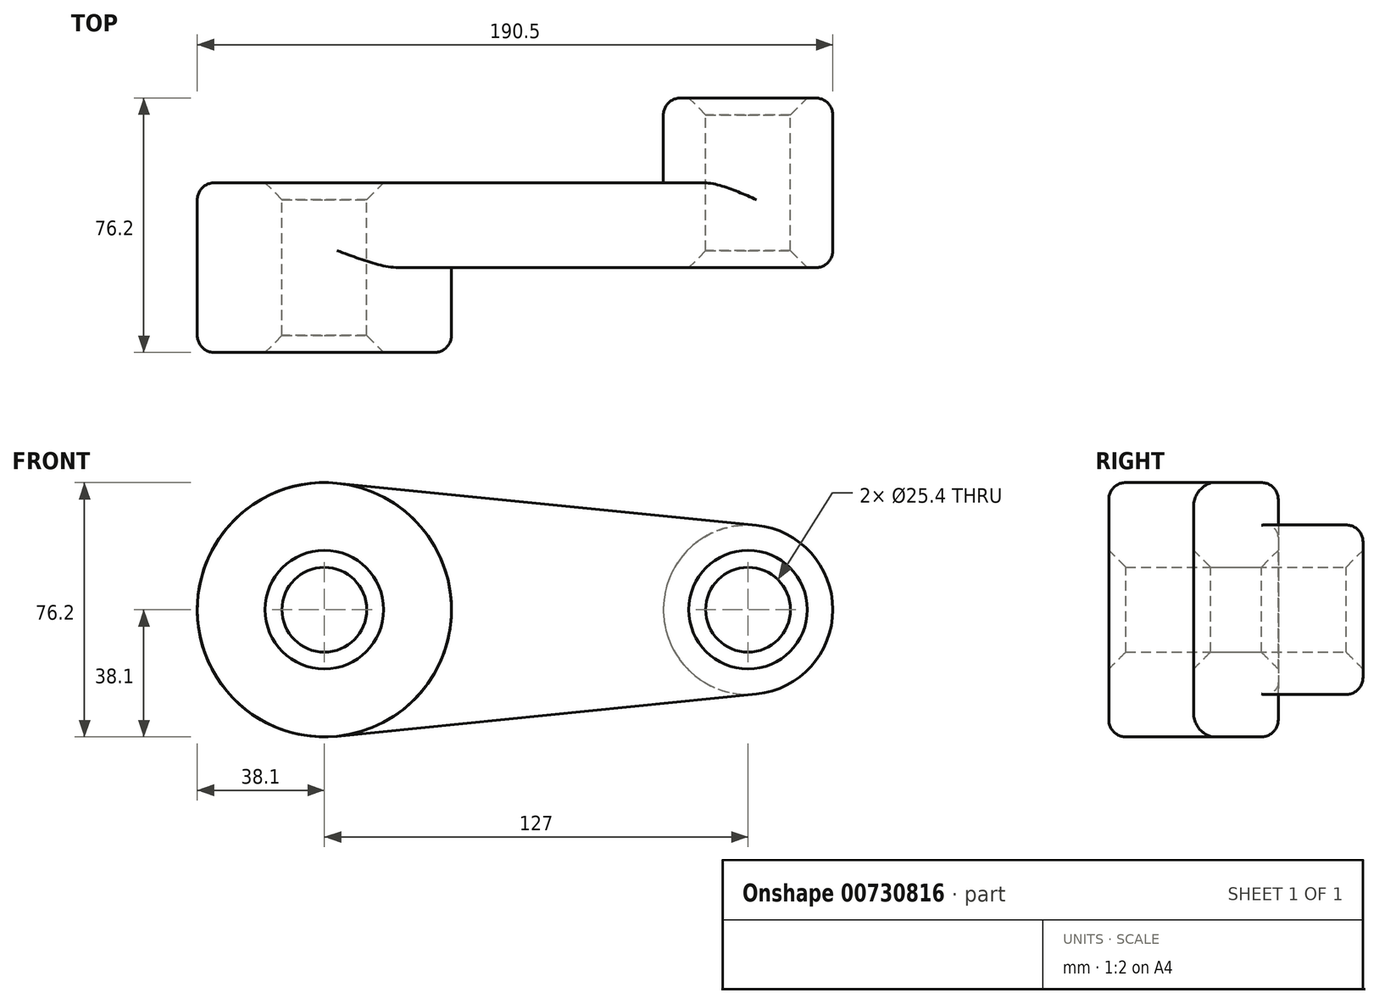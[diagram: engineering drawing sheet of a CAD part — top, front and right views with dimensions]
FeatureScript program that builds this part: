
annotation { "Feature Type Name" : "Feature", "Feature Type Description" : "" }
export const myFeature = defineFeature(function(context is Context, id is Id, definition is map)
    precondition{}
    {
        {
            var Q0;
            Q0=qCreatedBy(makeId("Front.planeOp"),FACE);
            var sketch = newSketch(context, id + "F0", { "sketchPlane" : qUnion([Q0])});
            skCircle(sketch, "E0", {"center": v(0, 0) * mm, "radius": 38.1 * mm});
            skCircle(sketch, "E1", {"center": v(127, 0) * mm, "radius": 25.4 * mm});
            skLineSegment(sketch, "E2", {"start": v(3.8, 37.9) * mm, "end": v(129.54, 25.27) * mm});
            skLineSegment(sketch, "E3", {"start": v(3.8, -37.9) * mm, "end": v(129.54, -25.27) * mm});
            skCircle(sketch, "E4", {"center": v(0, 0) * mm, "radius": 12.7 * mm});
            skCircle(sketch, "E5", {"center": v(127, 0) * mm, "radius": 12.7 * mm});
            skSolve(sketch);
        }
        {
            var Q0;
            Q0 = qSketchRegion(id + "F0", true);
            extrude(context, id + "F1", {"entities" : qUnion([Q0]), "depth" : 25.4 * mm, "offsetDistance" : 25.4 * mm});
        }
        {
            var Q0;
            Q0=makeQuery(id+"F0.imprint","IMPRINT",FACE,{"disambiguationData":[TD([[makeQuery(id+"F0.imprint","IMPRINT",EDGE,{"derivedFrom":sQuery(id+"F0.wireOp",EDGE,"E4")}),-1.0]])]});
            extrude(context, id + "F2", {"entities" : qUnion([Q0]), "operationType" : NewBodyOperationType.ADD, "depth" : 50.8 * mm, "offsetDistance" : 25.4 * mm});
        }
        {
            var Q0;
            Q0=makeQuery(id+"F1.opExtrude","CAP_EDGE",EDGE,{"disambiguationData":[OSD([sQuery(id+"F0.wireOp",EDGE,"E3")])],"isStart":false});
            fillet(context, id + "F3", {"entities" : qUnion([Q0]), "radius" : 5.08 * mm, "tangentPropagation" : true, "allowEdgeOverflow" : false});
        }
        {
            var Q0;
            Q0=makeQuery(id+"F2.opExtrude","CAP_EDGE",EDGE,{"disambiguationData":[OSD([sQuery(id+"F0.wireOp",EDGE,"E4")])],"isStart":false});
            var Q1;
            Q1=makeQuery(id+"F1.opExtrude","CAP_EDGE",EDGE,{"disambiguationData":[OSD([sQuery(id+"F0.wireOp",EDGE,"E5")])],"isStart":false});
            chamfer(context, id + "F4", {"entities" : qUnion([Q0, Q1]), "width" : 5.08 * mm, "tangentPropagation" : true});
        }
        {
            var Q0;
            Q0=makeQuery(id+"F0.imprint","IMPRINT",FACE,{"disambiguationData":[TD([[makeQuery(id+"F0.imprint","IMPRINT",EDGE,{"derivedFrom":sQuery(id+"F0.wireOp",EDGE,"E5")}),-1.0]])]});
            extrude(context, id + "F5", {"entities" : qUnion([Q0]), "operationType" : NewBodyOperationType.ADD, "oppositeDirection" : true, "depth" : 25.4 * mm, "offsetDistance" : 25.4 * mm});
        }
        {
            var Q0;
            Q0=makeQuery(id+"F5.opExtrude","CAP_EDGE",EDGE,{"disambiguationData":[OSD([sQuery(id+"F0.wireOp",EDGE,"E1")])],"isStart":false});
            fillet(context, id + "F6", {"entities" : qUnion([Q0]), "radius" : 5.08 * mm, "tangentPropagation" : true, "allowEdgeOverflow" : false});
        }
        {
            var Q0;
            Q0=makeQuery(id+"F1.opExtrude","CAP_EDGE",EDGE,{"disambiguationData":[OSD([sQuery(id+"F0.wireOp",EDGE,"E3")])],"isStart":true});
            fillet(context, id + "F7", {"entities" : qUnion([Q0]), "radius" : 5.08 * mm, "tangentPropagation" : true, "allowEdgeOverflow" : false});
        }
        {
            var Q0;
            Q0=makeQuery(id+"F2.opExtrude","CAP_EDGE",EDGE,{"disambiguationData":[OSD([sQuery(id+"F0.wireOp",EDGE,"E0")])],"isStart":false});
            fillet(context, id + "F8", {"entities" : qUnion([Q0]), "radius" : 5.08 * mm, "tangentPropagation" : true, "allowEdgeOverflow" : false});
        }
        {
            var Q0;
            Q0=makeQuery(id+"F1.opExtrude","CAP_EDGE",EDGE,{"disambiguationData":[OSD([sQuery(id+"F0.wireOp",EDGE,"E4")])],"isStart":true});
            var Q1;
            Q1=makeQuery(id+"F5.opExtrude","CAP_EDGE",EDGE,{"disambiguationData":[OSD([sQuery(id+"F0.wireOp",EDGE,"E5")])],"isStart":false});
            chamfer(context, id + "F9", {"entities" : qUnion([Q0, Q1]), "width" : 5.08 * mm, "tangentPropagation" : true});
        }
    });
